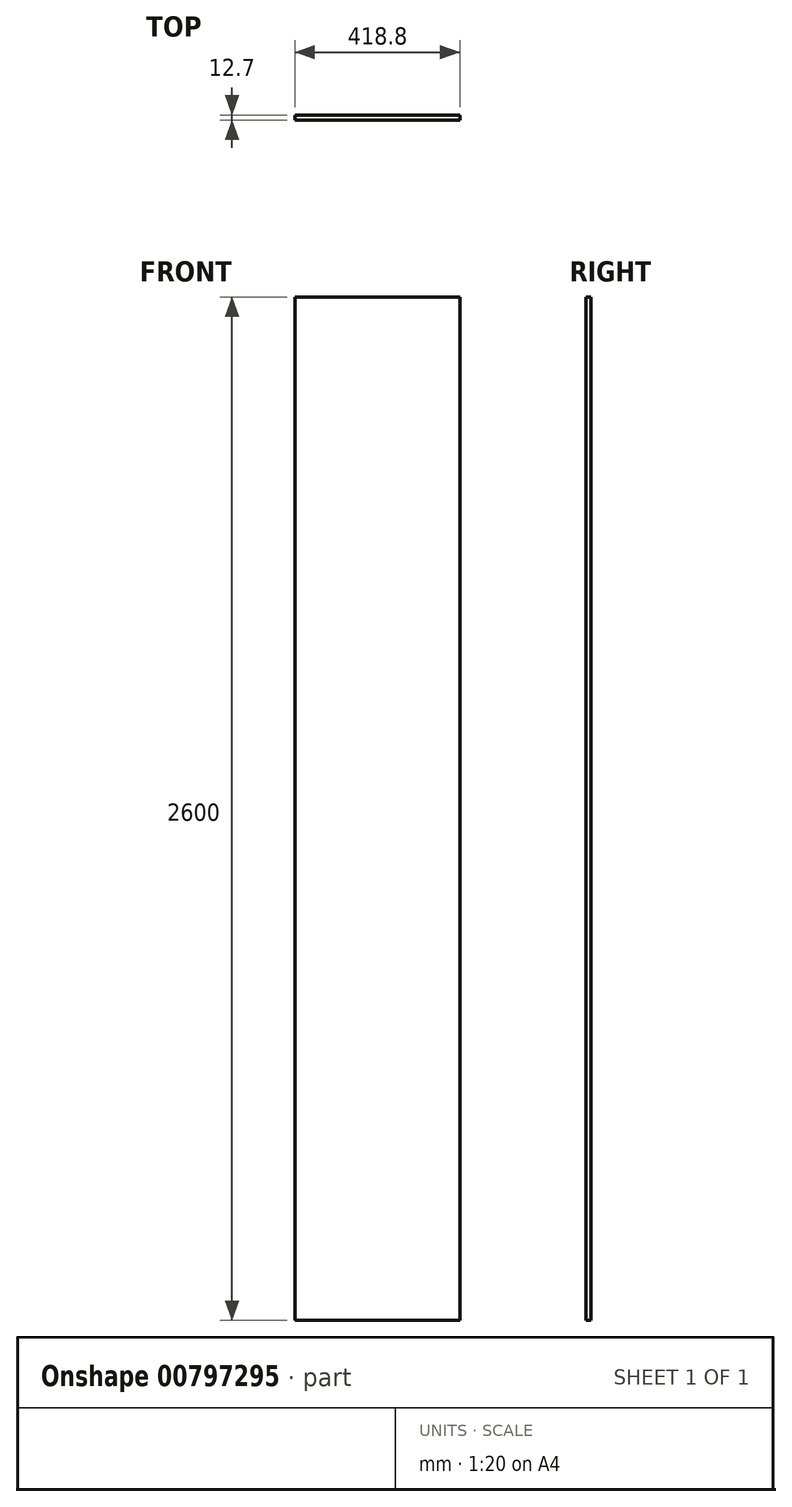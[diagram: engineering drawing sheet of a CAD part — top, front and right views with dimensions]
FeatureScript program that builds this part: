
annotation { "Feature Type Name" : "Feature", "Feature Type Description" : "" }
export const myFeature = defineFeature(function(context is Context, id is Id, definition is map)
    precondition{}
    {
        {
            var Q0;
            Q0=qCreatedBy(makeId("Front.planeOp"),FACE);
            var sketch = newSketch(context, id + "F0", { "sketchPlane" : qUnion([Q0])});
            skLineSegment(sketch, "E0.bottom", {"start": v(209.4, 1300) * mm, "end": v(-209.4, 1300) * mm});
            skLineSegment(sketch, "E0.top", {"start": v(209.4, -1300) * mm, "end": v(-209.4, -1300) * mm});
            skLineSegment(sketch, "E0.left", {"start": v(209.4, 1300) * mm, "end": v(209.4, -1300) * mm});
            skLineSegment(sketch, "E0.right", {"start": v(-209.4, 1300) * mm, "end": v(-209.4, -1300) * mm});
            skPoint(sketch, "E0.middle", {"position": v(0, 0) * mm});
            skSolve(sketch);
        }
        {
            var Q0;
            Q0 = qSketchRegion(id + "F0", true);
            extrude(context, id + "F1", {"entities" : qUnion([Q0]), "depth" : (25.4 / 2) * mm, "offsetDistance" : 25 * mm, "symmetric" : true});
        }
    });
